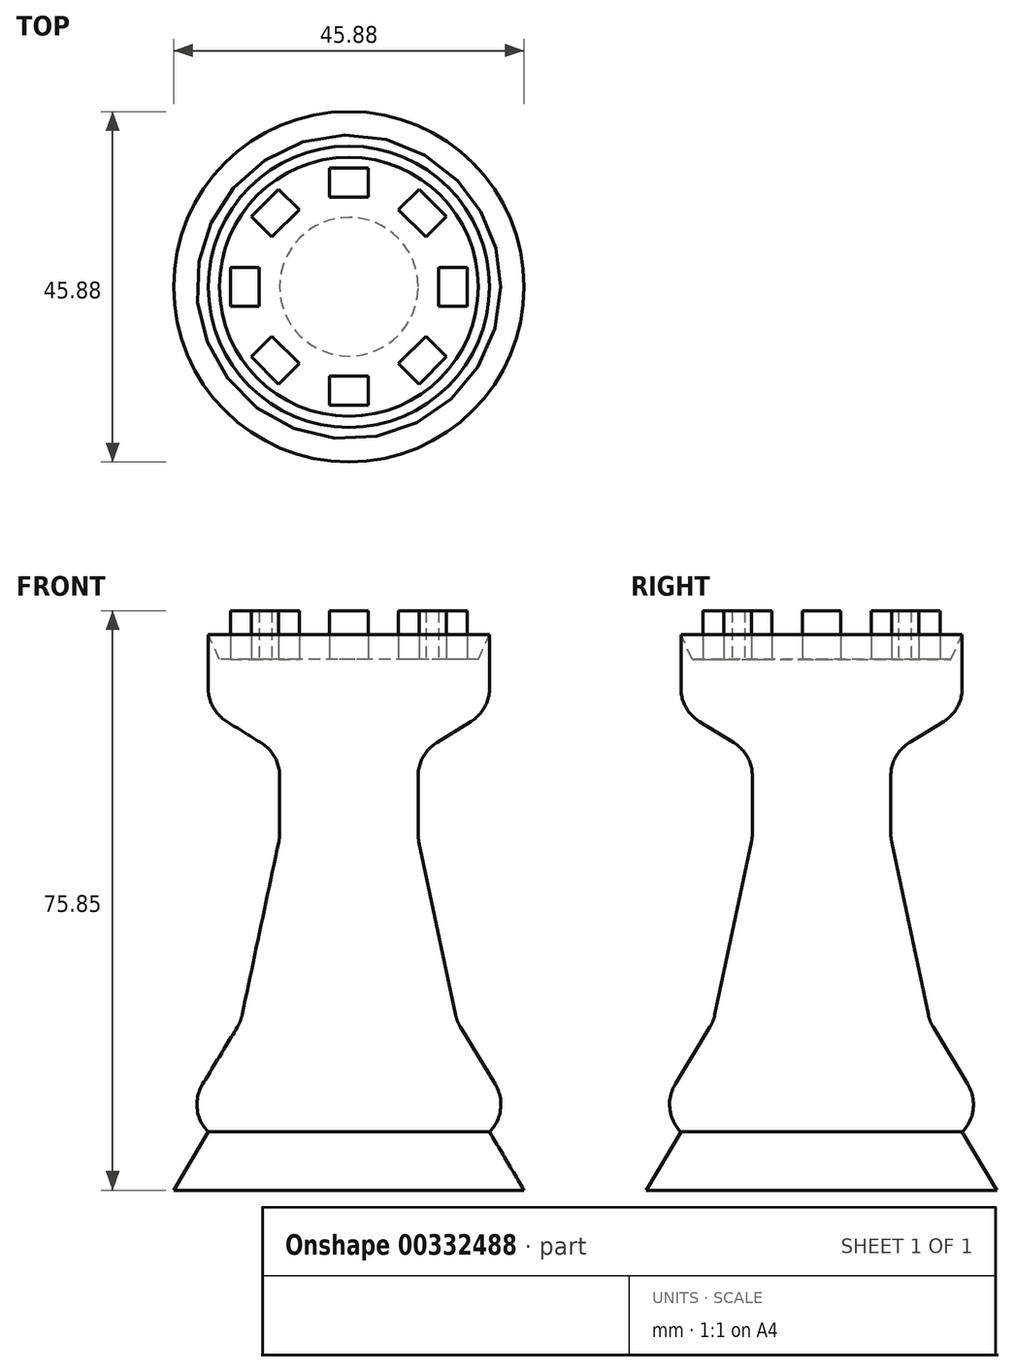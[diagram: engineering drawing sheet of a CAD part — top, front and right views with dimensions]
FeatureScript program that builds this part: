
annotation { "Feature Type Name" : "Feature", "Feature Type Description" : "" }
export const myFeature = defineFeature(function(context is Context, id is Id, definition is map)
    precondition{}
    {
        {
            var Q0;
            Q0=qCreatedBy(makeId("Front.planeOp"),FACE);
            var sketch = newSketch(context, id + "F0", { "sketchPlane" : qUnion([Q0])});
            skLineSegment(sketch, "E0", {"start": v(0, -57.07) * mm, "end": v(-22.94, -57.07) * mm});
            skLineSegment(sketch, "E1", {"start": v(-22.94, -57.07) * mm, "end": v(-18.4, -49.42) * mm});
            skLineSegment(sketch, "E2", {"start": v(-22.94, -49.42) * mm, "end": v(-18.4, -49.42) * mm});
            skLineSegment(sketch, "E3", {"start": v(-22.94, -49.42) * mm, "end": v(-14.16, -34.98) * mm});
            skLineSegment(sketch, "E4", {"start": v(-14.16, -34.98) * mm, "end": v(-9.06, -10.9) * mm});
            skLineSegment(sketch, "E5", {"start": v(-9.06, 0) * mm, "end": v(-9.06, -10.9) * mm});
            skLineSegment(sketch, "E6", {"start": v(-9.06, 0) * mm, "end": v(-18.4, 5.8) * mm});
            skLineSegment(sketch, "E7", {"start": v(-11.3, 12.43) * mm, "end": v(0, 12.43) * mm});
            skLineSegment(sketch, "E8", {"start": v(0, 12.43) * mm, "end": v(0, -57.07) * mm});
            skLineSegment(sketch, "E9", {"start": v(-18.4, 5.8) * mm, "end": v(-18.4, 15.7) * mm});
            skLineSegment(sketch, "E10", {"start": v(-11.3, 12.43) * mm, "end": v(-16.94, 12.43) * mm});
            skLineSegment(sketch, "E11", {"start": v(-16.94, 12.43) * mm, "end": v(-18.4, 15.7) * mm});
            skSolve(sketch);
        }
        {
            var Q0;
            Q0 = qSketchRegion(id + "F0", true);
            var Q1;
            Q1=makeQuery(id+"F0.imprint","IMPRINT",FACE,{"disambiguationData":[TD([[makeQuery(id+"F0.imprint","IMPRINT",EDGE,{"derivedFrom":sQuery(id+"F0.wireOp",EDGE,"E0")}),-1.0]])]});
            var Q2;
            Q2=sQuery(id+"F0.wireOp",EDGE,"E8");
            revolve(context, id + "F1", {"entities" : qUnion([Q0, Q1]), "axis" : qUnion([Q2]), "revolveType" : RevolveType.FULL});
        }
        {
            var Q0;
            Q0=makeQuery(id+"F1.opRevolve","SWEPT_FACE",FACE,{"disambiguationData":[OSD([sQuery(id+"F0.wireOp",EDGE,"E3")])]});
            var Q1;
            Q1=makeQuery(id+"F1.opRevolve","SWEPT_FACE",FACE,{"disambiguationData":[OSD([sQuery(id+"F0.wireOp",EDGE,"E4")])]});
            var Q2;
            Q2=makeQuery(id+"F1.opRevolve","SWEPT_FACE",FACE,{"disambiguationData":[OSD([sQuery(id+"F0.wireOp",EDGE,"E5")])]});
            var Q3;
            Q3=makeQuery(id+"F1.opRevolve","SWEPT_EDGE",EDGE,{"disambiguationData":[OSD([sQuery(id+"F0.wireOp",EDGE,"E6"),sQuery(id+"F0.wireOp",EDGE,"EsJSsOHj-wZSO-mz0q-MAMM-WpjJxJVHybRE")])]});
            fillet(context, id + "F2", {"entities" : qUnion([Q0, Q1, Q2, Q3]), "radius" : 5.08 * mm, "tangentPropagation" : true, "allowEdgeOverflow" : false});
        }
        {
            var Q0;
            Q0=makeQuery(id+"F1.opRevolve","SWEPT_FACE",FACE,{"disambiguationData":[OSD([sQuery(id+"F0.wireOp",EDGE,"E7"),sQuery(id+"F0.wireOp",EDGE,"E10")])]});
            var sketch = newSketch(context, id + "F3", { "sketchPlane" : qUnion([Q0])});
            skLineSegment(sketch, "E12.bottom", {"start": v(-15.52, 2.53) * mm, "end": v(-11.72, 2.53) * mm});
            skLineSegment(sketch, "E12.top", {"start": v(-15.52, -2.53) * mm, "end": v(-11.72, -2.53) * mm});
            skLineSegment(sketch, "E12.left", {"start": v(-15.52, 2.53) * mm, "end": v(-15.52, -2.53) * mm});
            skLineSegment(sketch, "E12.right", {"start": v(-11.72, 2.53) * mm, "end": v(-11.72, -2.53) * mm});
            skPoint(sketch, "E12.middle", {"position": v(-13.62, 0) * mm});
            skLineSegment(sketch, "E13.1.0", {"start": v(-12.76, -9.18) * mm, "end": v(-10.08, -6.5) * mm});
            skLineSegment(sketch, "E13.1.1", {"start": v(-10.08, -6.5) * mm, "end": v(-6.5, -10.08) * mm});
            skLineSegment(sketch, "E13.1.2", {"start": v(-9.18, -12.76) * mm, "end": v(-6.5, -10.08) * mm});
            skLineSegment(sketch, "E13.1.3", {"start": v(-12.76, -9.18) * mm, "end": v(-9.18, -12.76) * mm});
            skLineSegment(sketch, "E13.2.0", {"start": v(-2.53, -15.52) * mm, "end": v(-2.53, -11.72) * mm});
            skLineSegment(sketch, "E13.2.1", {"start": v(-2.53, -11.72) * mm, "end": v(2.53, -11.72) * mm});
            skLineSegment(sketch, "E13.2.2", {"start": v(2.53, -15.52) * mm, "end": v(2.53, -11.72) * mm});
            skLineSegment(sketch, "E13.2.3", {"start": v(-2.53, -15.52) * mm, "end": v(2.53, -15.52) * mm});
            skLineSegment(sketch, "E13.3.0", {"start": v(9.18, -12.76) * mm, "end": v(6.5, -10.08) * mm});
            skLineSegment(sketch, "E13.3.1", {"start": v(6.5, -10.08) * mm, "end": v(10.08, -6.5) * mm});
            skLineSegment(sketch, "E13.3.2", {"start": v(12.76, -9.18) * mm, "end": v(10.08, -6.5) * mm});
            skLineSegment(sketch, "E13.3.3", {"start": v(9.18, -12.76) * mm, "end": v(12.76, -9.18) * mm});
            skLineSegment(sketch, "E13.4.0", {"start": v(15.52, -2.53) * mm, "end": v(11.72, -2.53) * mm});
            skLineSegment(sketch, "E13.4.1", {"start": v(11.72, -2.53) * mm, "end": v(11.72, 2.53) * mm});
            skLineSegment(sketch, "E13.4.2", {"start": v(15.52, 2.53) * mm, "end": v(11.72, 2.53) * mm});
            skLineSegment(sketch, "E13.4.3", {"start": v(15.52, -2.53) * mm, "end": v(15.52, 2.53) * mm});
            skLineSegment(sketch, "E13.5.0", {"start": v(12.76, 9.18) * mm, "end": v(10.08, 6.5) * mm});
            skLineSegment(sketch, "E13.5.1", {"start": v(10.08, 6.5) * mm, "end": v(6.5, 10.08) * mm});
            skLineSegment(sketch, "E13.5.2", {"start": v(9.18, 12.76) * mm, "end": v(6.5, 10.08) * mm});
            skLineSegment(sketch, "E13.5.3", {"start": v(12.76, 9.18) * mm, "end": v(9.18, 12.76) * mm});
            skLineSegment(sketch, "E13.6.0", {"start": v(2.53, 15.52) * mm, "end": v(2.53, 11.72) * mm});
            skLineSegment(sketch, "E13.6.1", {"start": v(2.53, 11.72) * mm, "end": v(-2.53, 11.72) * mm});
            skLineSegment(sketch, "E13.6.2", {"start": v(-2.53, 15.52) * mm, "end": v(-2.53, 11.72) * mm});
            skLineSegment(sketch, "E13.6.3", {"start": v(2.53, 15.52) * mm, "end": v(-2.53, 15.52) * mm});
            skLineSegment(sketch, "E13.7.0", {"start": v(-9.18, 12.76) * mm, "end": v(-6.5, 10.08) * mm});
            skLineSegment(sketch, "E13.7.1", {"start": v(-6.5, 10.08) * mm, "end": v(-10.08, 6.5) * mm});
            skLineSegment(sketch, "E13.7.2", {"start": v(-12.76, 9.18) * mm, "end": v(-10.08, 6.5) * mm});
            skLineSegment(sketch, "E13.7.3", {"start": v(-9.18, 12.76) * mm, "end": v(-12.76, 9.18) * mm});
            skPoint(sketch, "E13.center", {"position": v(0, 0) * mm});
            skSolve(sketch);
        }
        {
            var Q0;
            Q0 = qSketchRegion(id + "F3", true);
            extrude(context, id + "F4", {"entities" : qUnion([Q0]), "operationType" : NewBodyOperationType.ADD, "depth" : 6.35 * mm, "offsetDistance" : 25.4 * mm});
        }
    });
